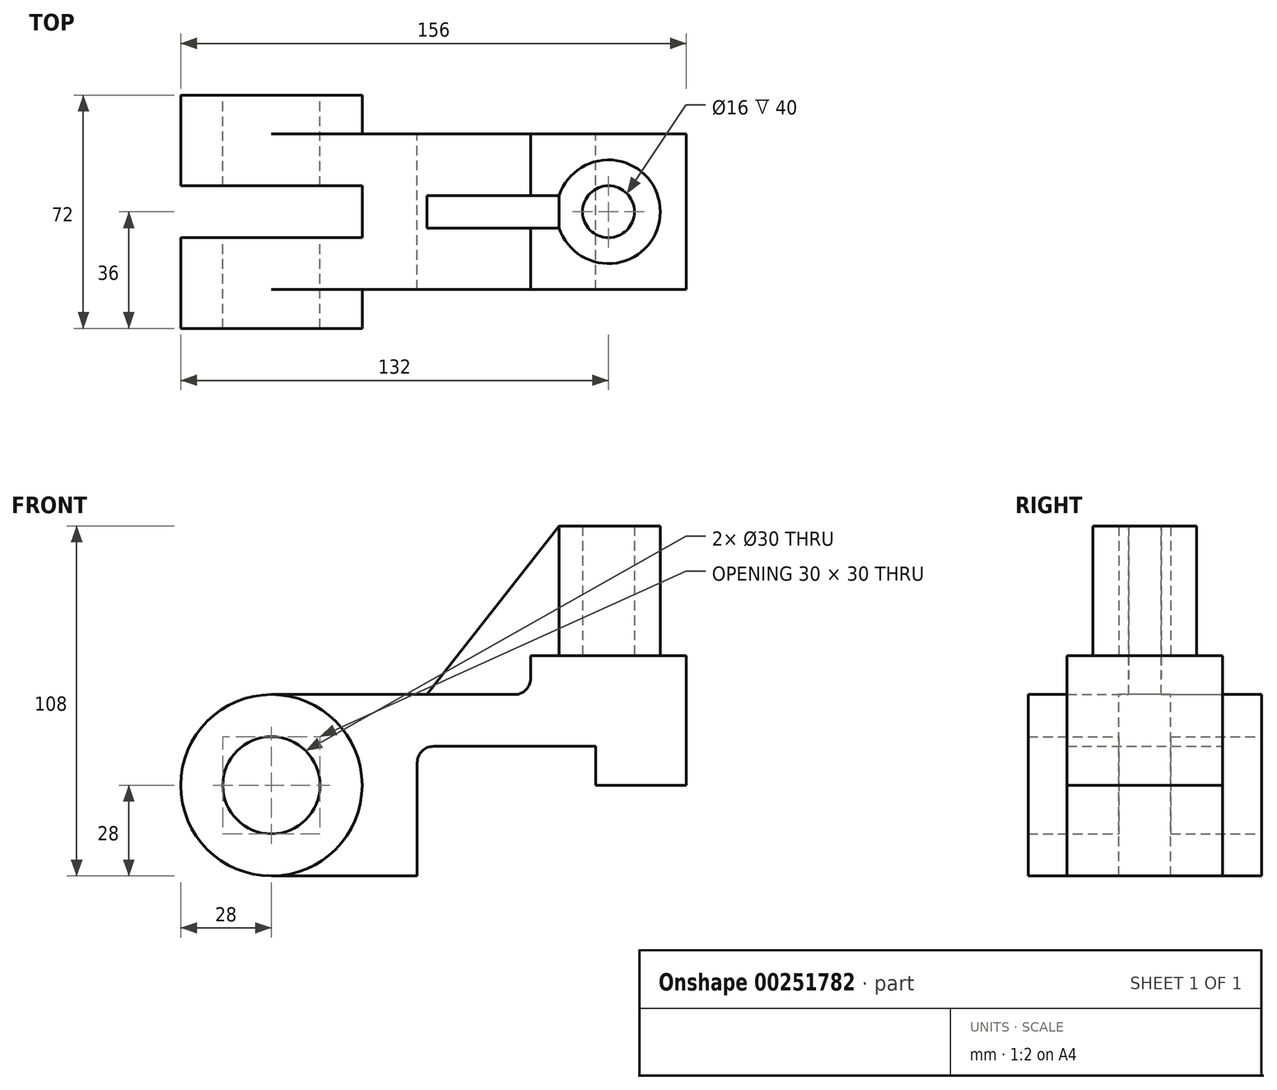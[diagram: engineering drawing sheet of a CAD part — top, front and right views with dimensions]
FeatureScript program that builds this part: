
annotation { "Feature Type Name" : "Feature", "Feature Type Description" : "" }
export const myFeature = defineFeature(function(context is Context, id is Id, definition is map)
    precondition{}
    {
        {
            var Q0;
            Q0=qCreatedBy(makeId("Front.planeOp"),FACE);
            var sketch = newSketch(context, id + "F0", { "sketchPlane" : qUnion([Q0])});
            skLineSegment(sketch, "E0", {"start": v(28, 0) * mm, "end": v(28, 40) * mm});
            skLineSegment(sketch, "E1", {"start": v(28, 40) * mm, "end": v(-20, 40) * mm});
            skLineSegment(sketch, "E2", {"start": v(28, 0) * mm, "end": v(0, 0) * mm});
            skLineSegment(sketch, "E3", {"start": v(0, 0) * mm, "end": v(0, 12) * mm});
            skLineSegment(sketch, "E4", {"start": v(0, 12) * mm, "end": v(-55, 12) * mm});
            skLineSegment(sketch, "E5", {"start": v(-20, 40) * mm, "end": v(-20, 28) * mm});
            skLineSegment(sketch, "E6", {"start": v(-20, 28) * mm, "end": v(-100, 28) * mm});
            skCircle(sketch, "E7", {"center": v(-100, 0) * mm, "radius": 28 * mm});
            skCircle(sketch, "E8", {"center": v(-100, 0) * mm, "radius": 15 * mm});
            skLineSegment(sketch, "E9", {"start": v(-55, 12) * mm, "end": v(-55, -28) * mm});
            skLineSegment(sketch, "E10", {"start": v(-55, -28) * mm, "end": v(-100, -28) * mm});
            skSolve(sketch);
        }
        {
            var Q0;
            Q0 = qSketchRegion(id + "F0", true);
            extrude(context, id + "F1", {"entities" : qUnion([Q0]), "endBound" : BoundingType.SYMMETRIC, "depth" : 48 * mm});
        }
        {
            var Q0;
            Q0=makeQuery(id+"F1.opExtrude","SWEPT_FACE",FACE,{"disambiguationData":[OSD([sQuery(id+"F0.wireOp",EDGE,"E6")])]});
            var sketch = newSketch(context, id + "F2", { "sketchPlane" : qUnion([Q0])});
            skLineSegment(sketch, "E11.bottom", {"start": v(-72, 8) * mm, "end": v(-128, 8) * mm});
            skLineSegment(sketch, "E11.top", {"start": v(-72, -8) * mm, "end": v(-128, -8) * mm});
            skLineSegment(sketch, "E11.left", {"start": v(-72, 8) * mm, "end": v(-72, -8) * mm});
            skLineSegment(sketch, "E11.right", {"start": v(-128, 8) * mm, "end": v(-128, -8) * mm});
            skPoint(sketch, "E11.middle", {"position": v(-100, 0) * mm});
            skLineSegment(sketch, "E12.0", {"start": v(-100, -24) * mm, "end": v(-100, 24) * mm});
            skSolve(sketch);
        }
        {
            var Q0;
            Q0 = qSketchRegion(id + "F2", true);
            extrude(context, id + "F3", {"entities" : qUnion([Q0]), "operationType" : NewBodyOperationType.REMOVE, "endBound" : BoundingType.THROUGH_ALL, "oppositeDirection" : true, "depth" : 25 * mm});
        }
        {
            var Q0;
            Q0=makeQuery(id+"F1.opExtrude","CAP_FACE",FACE,{"disambiguationData":[OSD([sQuery(id+"F0.wireOp",EDGE,"E0"),sQuery(id+"F0.wireOp",EDGE,"E1"),sQuery(id+"F0.wireOp",EDGE,"E2"),sQuery(id+"F0.wireOp",EDGE,"E3"),sQuery(id+"F0.wireOp",EDGE,"E4"),sQuery(id+"F0.wireOp",EDGE,"E5"),sQuery(id+"F0.wireOp",EDGE,"E6"),sQuery(id+"F0.wireOp",EDGE,"E7"),sQuery(id+"F0.wireOp",EDGE,"E8"),sQuery(id+"F0.wireOp",EDGE,"E9"),sQuery(id+"F0.wireOp",EDGE,"E10")])],"isStart":false});
            var sketch = newSketch(context, id + "F4", { "sketchPlane" : qUnion([Q0])});
            skCircle(sketch, "E13", {"center": v(-100, 0) * mm, "radius": 28 * mm});
            skCircle(sketch, "E14", {"center": v(-100, 0) * mm, "radius": 15 * mm});
            skSolve(sketch);
        }
        {
            var Q0;
            Q0 = qSketchRegion(id + "F4", true);
            extrude(context, id + "F5", {"entities" : qUnion([Q0]), "operationType" : NewBodyOperationType.ADD, "depth" : 12 * mm});
        }
        {
            var Q0;
            Q0=makeQuery(id+"F1.opExtrude","CAP_FACE",FACE,{"disambiguationData":[OSD([sQuery(id+"F0.wireOp",EDGE,"E0"),sQuery(id+"F0.wireOp",EDGE,"E1"),sQuery(id+"F0.wireOp",EDGE,"E2"),sQuery(id+"F0.wireOp",EDGE,"E3"),sQuery(id+"F0.wireOp",EDGE,"E4"),sQuery(id+"F0.wireOp",EDGE,"E5"),sQuery(id+"F0.wireOp",EDGE,"E6"),sQuery(id+"F0.wireOp",EDGE,"E7"),sQuery(id+"F0.wireOp",EDGE,"E8"),sQuery(id+"F0.wireOp",EDGE,"E9"),sQuery(id+"F0.wireOp",EDGE,"E10")])],"isStart":true});
            var sketch = newSketch(context, id + "F6", { "sketchPlane" : qUnion([Q0])});
            skCircle(sketch, "E15", {"center": v(100, 0) * mm, "radius": 28 * mm});
            skCircle(sketch, "E16", {"center": v(100, 0) * mm, "radius": 15 * mm});
            skSolve(sketch);
        }
        {
            var Q0;
            Q0 = qSketchRegion(id + "F6", true);
            extrude(context, id + "F7", {"entities" : qUnion([Q0]), "operationType" : NewBodyOperationType.ADD, "depth" : 12 * mm});
        }
        {
            var Q0;
            Q0=makeQuery(id+"F1.opExtrude","SWEPT_EDGE",EDGE,{"disambiguationData":[OSD([sQuery(id+"F0.wireOp",EDGE,"E4"),sQuery(id+"F0.wireOp",EDGE,"E9")])]});
            fillet(context, id + "F8", {"entities" : qUnion([Q0]), "radius" : 5 * mm, "tangentPropagation" : true, "allowEdgeOverflow" : false});
        }
        {
            var Q0;
            Q0=makeQuery(id+"F1.opExtrude","SWEPT_EDGE",EDGE,{"disambiguationData":[OSD([sQuery(id+"F0.wireOp",EDGE,"E5"),sQuery(id+"F0.wireOp",EDGE,"E6")])]});
            fillet(context, id + "F9", {"entities" : qUnion([Q0]), "radius" : 5 * mm, "tangentPropagation" : true, "allowEdgeOverflow" : false});
        }
        {
            var Q0;
            Q0=makeQuery(id+"F1.opExtrude","SWEPT_FACE",FACE,{"disambiguationData":[OSD([sQuery(id+"F0.wireOp",EDGE,"E1")])]});
            var sketch = newSketch(context, id + "F10", { "sketchPlane" : qUnion([Q0])});
            skCircle(sketch, "E17", {"center": v(4, 0) * mm, "radius": 16 * mm});
            skPoint(sketch, "E17.centerSnap0", {"position": v(4, 24) * mm});
            skCircle(sketch, "E18", {"center": v(4, 0) * mm, "radius": 8 * mm});
            skSolve(sketch);
        }
        {
            var Q0;
            Q0 = qSketchRegion(id + "F10", true);
            extrude(context, id + "F11", {"entities" : qUnion([Q0]), "operationType" : NewBodyOperationType.ADD, "depth" : 40 * mm});
        }
        {
            var Q0;
            Q0=makeQuery(id+"F1.opExtrude","SWEPT_FACE",FACE,{"disambiguationData":[OSD([sQuery(id+"F0.wireOp",EDGE,"E6")])]});
            var sketch = newSketch(context, id + "F12", { "sketchPlane" : qUnion([Q0])});
            skLineSegment(sketch, "E19.bottom", {"start": v(-11.2, -5) * mm, "end": v(-52, -5) * mm});
            skLineSegment(sketch, "E19.top", {"start": v(-11.2, 5) * mm, "end": v(-52, 5) * mm});
            skPoint(sketch, "E19.middle", {"position": v(-43.71, 0) * mm});
            skLineSegment(sketch, "E20", {"start": v(-52, 5) * mm, "end": v(-52, -5) * mm});
            skArc(sketch, "E21.0", {"start": v(-11.2, 5) * mm, "mid": v(-12, 0) * mm, "end": v(-11.2, -5) * mm});
            skPoint(sketch, "E19.right.end.orphan", {"position": v(-81.95, 5) * mm});
            skPoint(sketch, "E19.right.start.orphan", {"position": v(-81.95, -5) * mm});
            skPoint(sketch, "E19.left.start.orphan", {"position": v(-5.48, -5) * mm});
            skPoint(sketch, "E22.orphan", {"position": v(-5.48, 5) * mm});
            skSolve(sketch);
        }
        {
            var Q0;
            Q0 = qSketchRegion(id + "F12", true);
            extrude(context, id + "F13", {"entities" : qUnion([Q0]), "operationType" : NewBodyOperationType.ADD, "depth" : 52 * mm});
        }
        {
            var Q0;
            Q0=makeQuery(id+"F13.opExtrude","SWEPT_FACE",FACE,{"disambiguationData":[OSD([sQuery(id+"F12.wireOp",EDGE,"E19.bottom")])]});
            var sketch = newSketch(context, id + "F14", { "sketchPlane" : qUnion([Q0])});
            skLineSegment(sketch, "E23", {"start": v(-52, 28) * mm, "end": v(-11.2, 80) * mm});
            skLineSegment(sketch, "E24.0", {"start": v(-11.2, 80) * mm, "end": v(-52, 80) * mm});
            skLineSegment(sketch, "E25.0", {"start": v(-52, 80) * mm, "end": v(-52, 28) * mm});
            skSolve(sketch);
        }
        {
            var Q0;
            Q0 = qSketchRegion(id + "F14", true);
            extrude(context, id + "F15", {"entities" : qUnion([Q0]), "operationType" : NewBodyOperationType.REMOVE, "endBound" : BoundingType.THROUGH_ALL, "oppositeDirection" : true, "depth" : 25 * mm});
        }
    });
